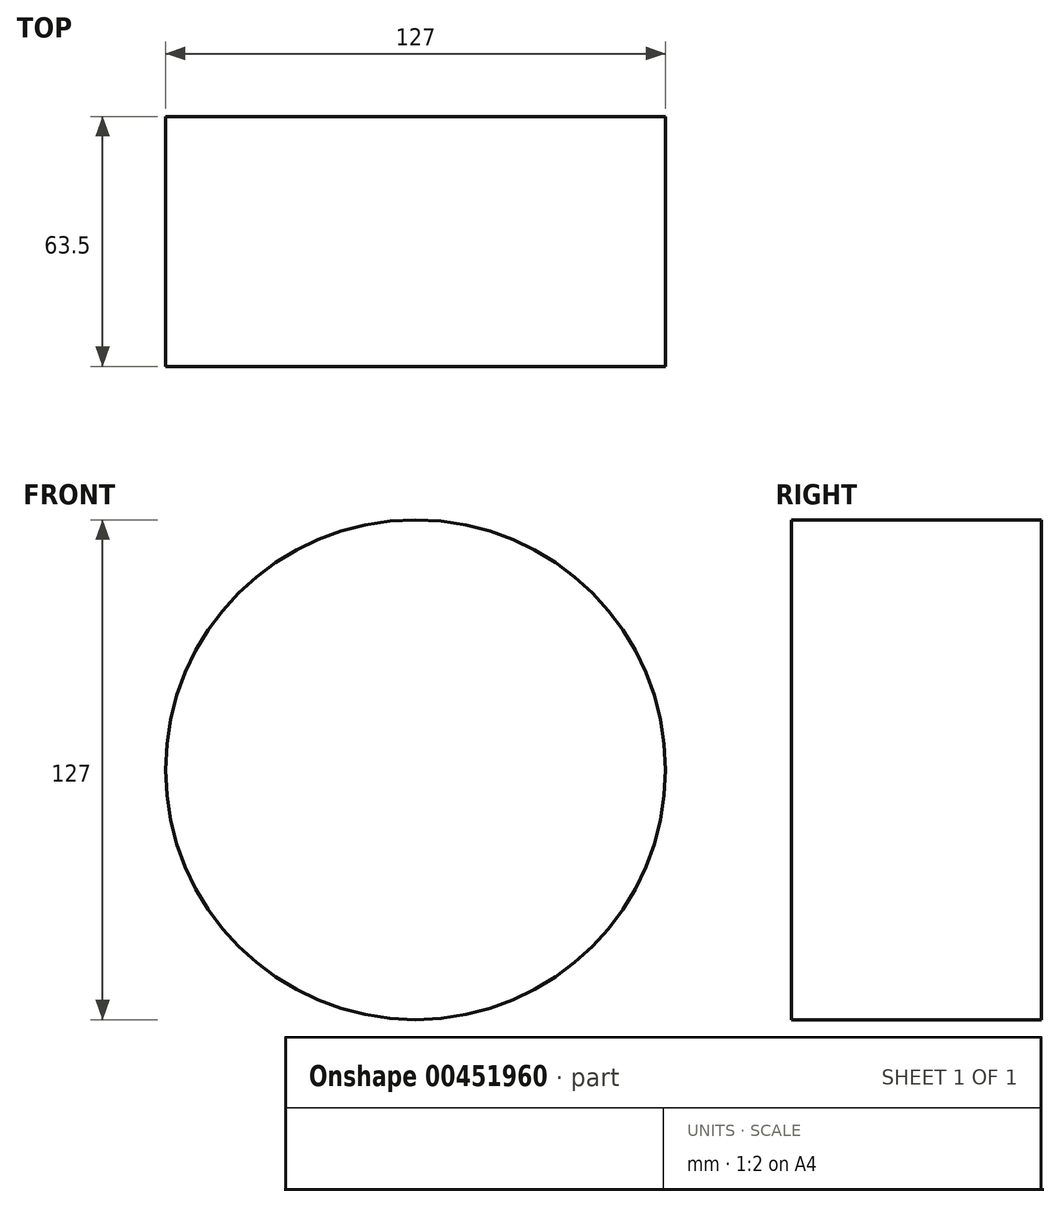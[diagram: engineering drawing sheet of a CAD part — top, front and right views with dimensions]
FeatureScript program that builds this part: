
annotation { "Feature Type Name" : "Feature", "Feature Type Description" : "" }
export const myFeature = defineFeature(function(context is Context, id is Id, definition is map)
    precondition{}
    {
        {
            var Q0;
            Q0=qCreatedBy(makeId("Front.planeOp"),FACE);
            var sketch = newSketch(context, id + "F0", { "sketchPlane" : qUnion([Q0])});
            skCircle(sketch, "E0", {"center": v(0, 0) * mm, "radius": 63.5 * mm});
            skSolve(sketch);
        }
        {
            var Q0;
            Q0=makeQuery(id+"F0.imprint","IMPRINT",FACE,{"disambiguationData":[TD([[makeQuery(id+"F0.imprint","IMPRINT",EDGE,{"derivedFrom":sQuery(id+"F0.wireOp",EDGE,"E0")}),1.0]])]});
            extrude(context, id + "F1", {"entities" : qUnion([Q0]), "depth" : 63.5 * mm});
        }
    });
